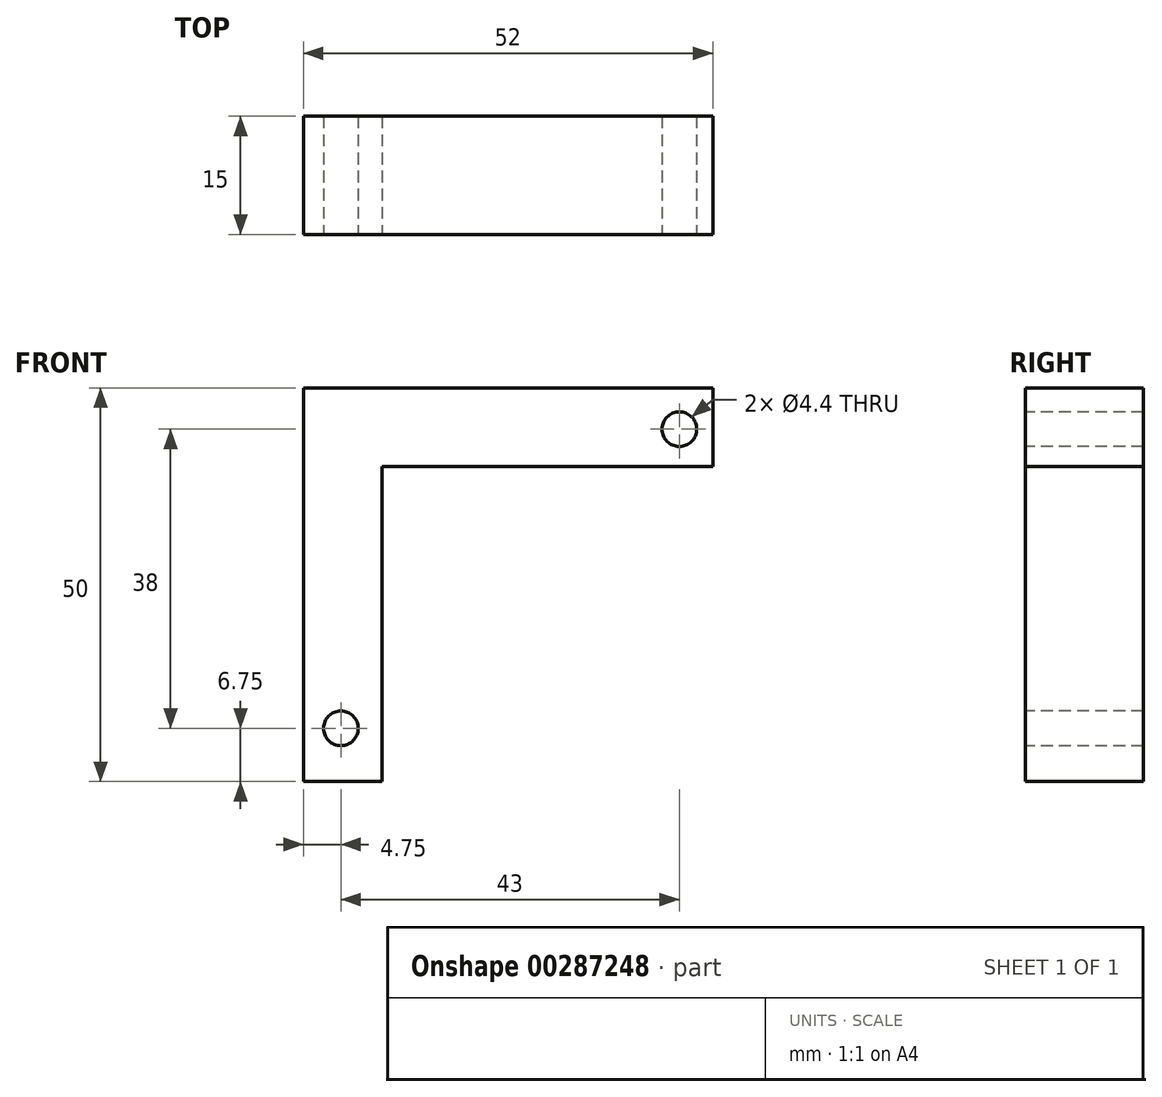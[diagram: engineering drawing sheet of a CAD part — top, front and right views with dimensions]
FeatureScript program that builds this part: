
annotation { "Feature Type Name" : "Feature", "Feature Type Description" : "" }
export const myFeature = defineFeature(function(context is Context, id is Id, definition is map)
    precondition{}
    {
        {
            var Q0;
            Q0=qCreatedBy(makeId("Front.planeOp"),FACE);
            var sketch = newSketch(context, id + "F0", { "sketchPlane" : qUnion([Q0])});
            skLineSegment(sketch, "E0.top", {"start": v(25.75, -25.75) * mm, "end": v(8.6, -25.75) * mm});
            skLineSegment(sketch, "E0.left", {"start": v(25.75, 0) * mm, "end": v(25.75, -25.75) * mm});
            skPoint(sketch, "E0.middle", {"position": v(0, 0) * mm});
            skArc(sketch, "E1", {"start": v(25.75, 0) * mm, "mid": v(24.57, 7.7) * mm, "end": v(21.15, 14.69) * mm});
            skArc(sketch, "E2", {"start": v(-25.75, 0) * mm, "mid": v(-24.55, -7.67) * mm, "end": v(-21.05, -14.6) * mm});
            skLineSegment(sketch, "E3", {"start": v(8.6, -25.75) * mm, "end": v(8.6, -23.19) * mm});
            skCircle(sketch, "E4", {"center": v(21.5, 19) * mm, "radius": 2.2 * mm});
            skCircle(sketch, "E5", {"center": v(-21.5, -19) * mm, "radius": 2.2 * mm});
            skArc(sketch, "E6", {"start": v(-23.49, -16.75) * mm, "mid": v(-23.75, -20.99) * mm, "end": v(-19.51, -21.25) * mm});
            skArc(sketch, "E7", {"start": v(23.49, 16.75) * mm, "mid": v(23.75, 20.99) * mm, "end": v(19.51, 21.25) * mm});
            skLineSegment(sketch, "E8", {"start": v(-23.49, -16.75) * mm, "end": v(-21.05, -14.6) * mm});
            skLineSegment(sketch, "E9", {"start": v(-19.51, -21.25) * mm, "end": v(-16.98, -19.01) * mm});
            skLineSegment(sketch, "E10", {"start": v(-21.5, -19) * mm, "end": v(21.5, 19) * mm, "construction": true});
            skArc(sketch, "E11.trimOffspring", {"start": v(-16.98, -19.01) * mm, "mid": v(-4.78, -24.67) * mm, "end": v(8.6, -23.19) * mm});
            skLineSegment(sketch, "E12", {"start": v(19.51, 21.25) * mm, "end": v(17.18, 19.18) * mm});
            skLineSegment(sketch, "E13", {"start": v(23.49, 16.75) * mm, "end": v(21.15, 14.69) * mm});
            skArc(sketch, "E14.trimOffspring", {"start": v(17.18, 19.18) * mm, "mid": v(-10.5, 23.5) * mm, "end": v(-25.75, 0) * mm});
            skSolve(sketch);
        }
        {
            var Q0;
            Q0=makeQuery(id+"F0.imprint","IMPRINT",FACE,{"disambiguationData":[TD([[makeQuery(id+"F0.imprint","IMPRINT",EDGE,{"derivedFrom":sQuery(id+"F0.wireOp",EDGE,"E0.top")}),-1.0]])]});
            extrude(context, id + "F1", {"entities" : qUnion([Q0]), "depth" : 15 * mm});
        }
        {
            var Q0;
            Q0=qCreatedBy(makeId("Front.planeOp"),FACE);
            var sketch = newSketch(context, id + "F2", { "sketchPlane" : qUnion([Q0])});
            skCircle(sketch, "E15.0", {"center": v(21.5, 19) * mm, "radius": 2.2 * mm});
            skCircle(sketch, "E16.0", {"center": v(-21.5, -19) * mm, "radius": 2.2 * mm});
            skLineSegment(sketch, "E17.top", {"start": v(25.75, 24.25) * mm, "end": v(-26.25, 24.25) * mm});
            skLineSegment(sketch, "E17.left", {"start": v(25.75, 14.25) * mm, "end": v(25.75, 24.25) * mm});
            skLineSegment(sketch, "E17.right", {"start": v(-26.25, -25.75) * mm, "end": v(-26.25, 24.25) * mm});
            skLineSegment(sketch, "E18", {"start": v(25.75, 14.25) * mm, "end": v(-16.25, 14.25) * mm});
            skLineSegment(sketch, "E19", {"start": v(-16.25, 14.25) * mm, "end": v(-16.25, -25.75) * mm});
            skLineSegment(sketch, "E20.trimOffspring", {"start": v(-16.25, -25.75) * mm, "end": v(-26.25, -25.75) * mm});
            skLineSegment(sketch, "E21.0", {"start": v(25.75, -25.75) * mm, "end": v(8.6, -25.75) * mm});
            skLineSegment(sketch, "E22.0.0", {"start": v(25.75, -25.75) * mm, "end": v(25.75, 0) * mm});
            skLineSegment(sketch, "E22.0.2", {"start": v(25.75, 0) * mm, "end": v(25.75, -25.75) * mm});
            skSolve(sketch);
        }
        {
            var Q0;
            Q0=makeQuery(id+"F2.imprint","IMPRINT",FACE,{"disambiguationData":[TD([[makeQuery(id+"F2.imprint","IMPRINT",EDGE,{"derivedFrom":sQuery(id+"F2.wireOp",EDGE,"E15.0")}),-1.0]])]});
            extrude(context, id + "F3", {"entities" : qUnion([Q0]), "oppositeDirection" : true, "depth" : 15 * mm});
        }
        {
            var Q0;
            Q0=makeQuery(id+"F1.opExtrude","SWEPT_BODY",BODY,{"disambiguationData":[OSD([sQuery(id+"F0.wireOp",EDGE,"E0.top"),sQuery(id+"F0.wireOp",EDGE,"E0.left"),sQuery(id+"F0.wireOp",EDGE,"E1"),sQuery(id+"F0.wireOp",EDGE,"E2"),sQuery(id+"F0.wireOp",EDGE,"E3"),sQuery(id+"F0.wireOp",EDGE,"E4"),sQuery(id+"F0.wireOp",EDGE,"E5"),sQuery(id+"F0.wireOp",EDGE,"E6"),sQuery(id+"F0.wireOp",EDGE,"E7"),sQuery(id+"F0.wireOp",EDGE,"E8"),sQuery(id+"F0.wireOp",EDGE,"E9"),sQuery(id+"F0.wireOp",EDGE,"E11.trimOffspring"),sQuery(id+"F0.wireOp",EDGE,"E12"),sQuery(id+"F0.wireOp",EDGE,"E13"),sQuery(id+"F0.wireOp",EDGE,"E14.trimOffspring")])]});
            deleteBodies(context, id + "F4", {"entities" : qUnion([Q0])});
        }
    });
